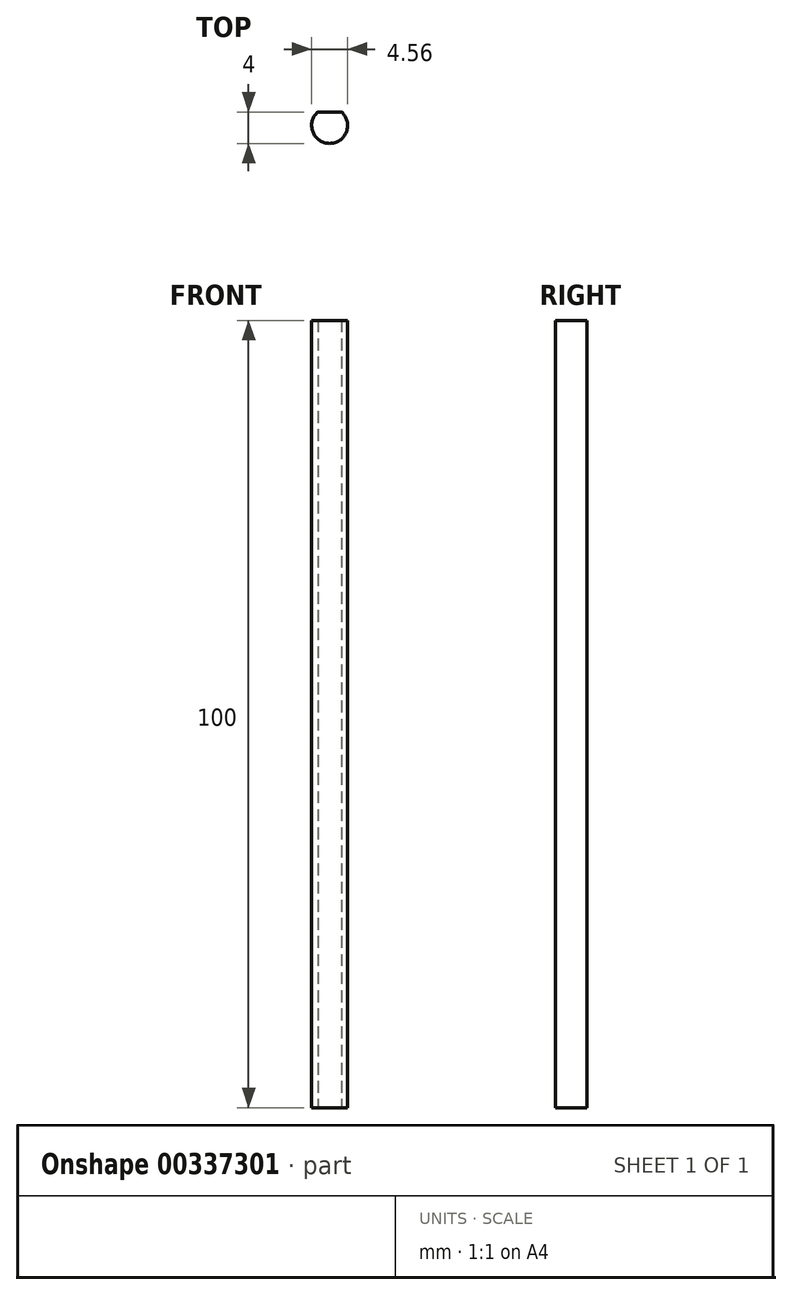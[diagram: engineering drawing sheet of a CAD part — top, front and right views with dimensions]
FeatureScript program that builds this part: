
annotation { "Feature Type Name" : "Feature", "Feature Type Description" : "" }
export const myFeature = defineFeature(function(context is Context, id is Id, definition is map)
    precondition{}
    {
        {
            var Q0;
            Q0=qCreatedBy(makeId("Top.planeOp"),FACE);
            var sketch = newSketch(context, id + "F0", { "sketchPlane" : qUnion([Q0])});
            skLineSegment(sketch, "E0", {"start": v(-1.5, 1.72) * mm, "end": v(1.5, 1.72) * mm});
            skArc(sketch, "E1", {"start": v(-1.5, 1.72) * mm, "mid": v(0, -2.28) * mm, "end": v(1.5, 1.72) * mm});
            skSolve(sketch);
        }
        {
            var Q0;
            Q0=makeQuery(id+"F0.imprint","IMPRINT",FACE,{"disambiguationData":[TD([[makeQuery(id+"F0.imprint","IMPRINT",EDGE,{"derivedFrom":sQuery(id+"F0.wireOp",EDGE,"E0")}),-1.0]])]});
            extrude(context, id + "F1", {"entities" : qUnion([Q0]), "depth" : 100 * mm});
        }
    });
